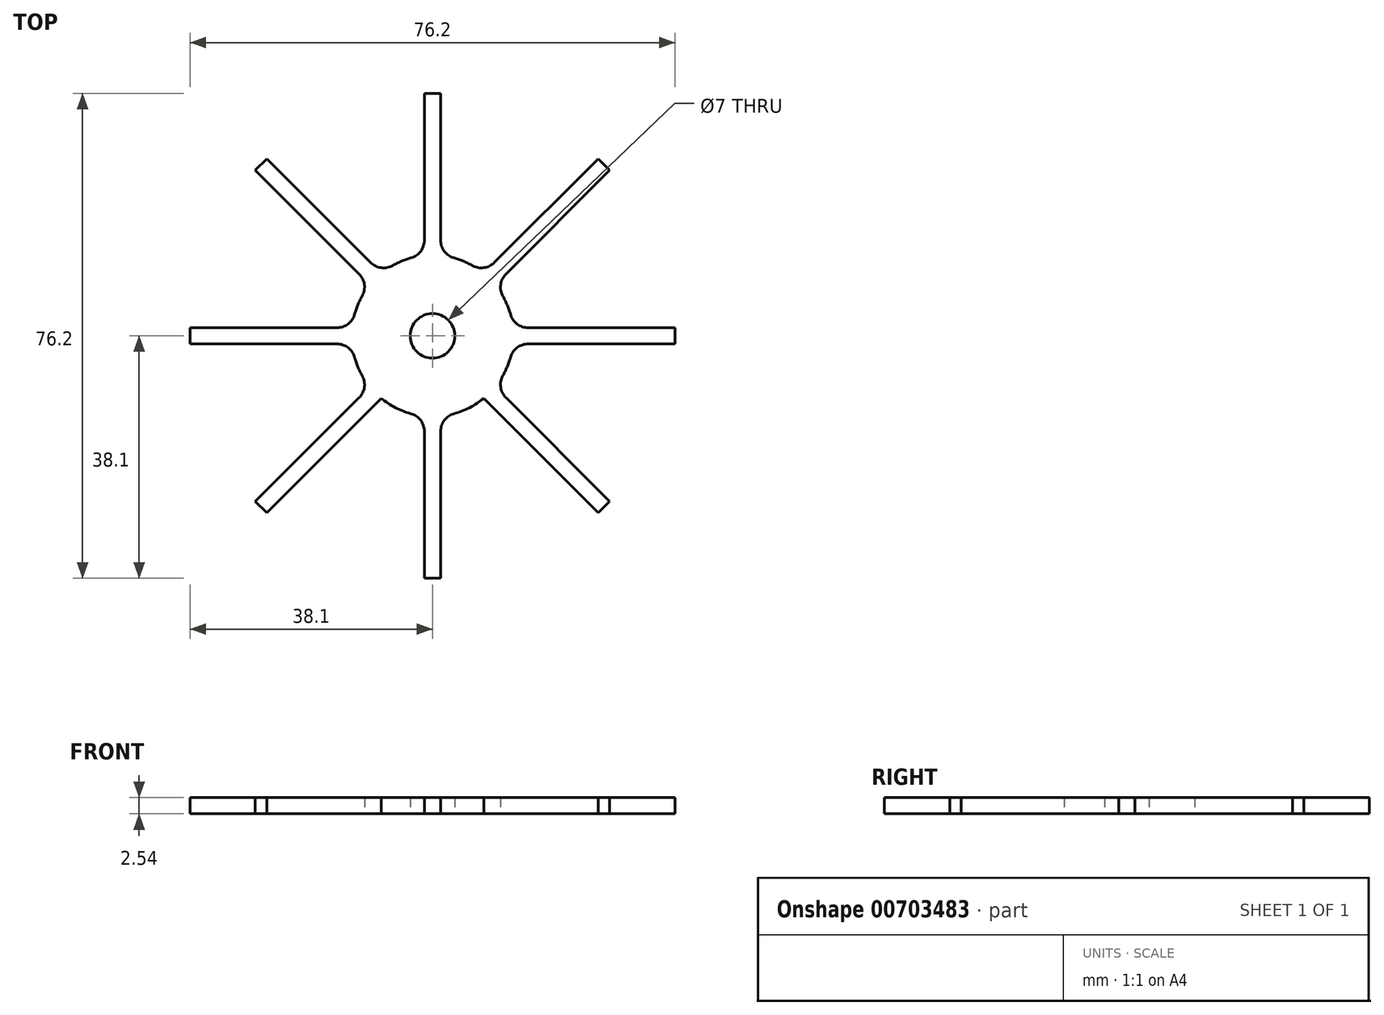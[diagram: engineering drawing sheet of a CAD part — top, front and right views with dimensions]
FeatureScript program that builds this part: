
annotation { "Feature Type Name" : "Feature", "Feature Type Description" : "" }
export const myFeature = defineFeature(function(context is Context, id is Id, definition is map)
    precondition{}
    {
        {
            var Q0;
            Q0=qCreatedBy(makeId("Top.planeOp"),FACE);
            var sketch = newSketch(context, id + "F0", { "sketchPlane" : qUnion([Q0])});
            skCircle(sketch, "E0", {"center": v(0, 0) * mm, "radius": 12.7 * mm});
            skSolve(sketch);
        }
        {
            var Q0;
            Q0=makeQuery(id+"F0.imprint","IMPRINT",FACE,{"disambiguationData":[TD([[makeQuery(id+"F0.imprint","IMPRINT",EDGE,{"derivedFrom":sQuery(id+"F0.wireOp",EDGE,"E0")}),1.0]])]});
            extrude(context, id + "F1", {"entities" : qUnion([Q0]), "depth" : 2.54 * mm, "offsetDistance" : 25.4 * mm});
        }
        {
            var Q0;
            Q0=qCreatedBy(makeId("Top.planeOp"),FACE);
            var sketch = newSketch(context, id + "F2", { "sketchPlane" : qUnion([Q0])});
            skLineSegment(sketch, "E1.bottom", {"start": v(-1.27, -38.1) * mm, "end": v(1.27, -38.1) * mm});
            skLineSegment(sketch, "E1.top", {"start": v(-1.27, 38.1) * mm, "end": v(1.27, 38.1) * mm});
            skLineSegment(sketch, "E1.left", {"start": v(-1.27, -38.1) * mm, "end": v(-1.27, 38.1) * mm});
            skLineSegment(sketch, "E1.right", {"start": v(1.27, -38.1) * mm, "end": v(1.27, 38.1) * mm});
            skPoint(sketch, "E1.middle", {"position": v(0, 0) * mm});
            skSolve(sketch);
        }
        {
            var Q0;
            Q0=makeQuery(id+"F2.imprint","IMPRINT",FACE,{"disambiguationData":[TD([[makeQuery(id+"F2.imprint","IMPRINT",EDGE,{"derivedFrom":sQuery(id+"F2.wireOp",EDGE,"E1.bottom")}),1.0]])]});
            extrude(context, id + "F3", {"entities" : qUnion([Q0]), "operationType" : NewBodyOperationType.ADD, "depth" : 2.54 * mm, "offsetDistance" : 25.4 * mm});
        }
        {
            var Q0;
            Q0=qCreatedBy(makeId("Top.planeOp"),FACE);
            var sketch = newSketch(context, id + "F4", { "sketchPlane" : qUnion([Q0])});
            skLineSegment(sketch, "E2.bottom", {"start": v(-38.1, -1.27) * mm, "end": v(38.1, -1.27) * mm});
            skLineSegment(sketch, "E2.top", {"start": v(-38.1, 1.27) * mm, "end": v(38.1, 1.27) * mm});
            skLineSegment(sketch, "E2.left", {"start": v(-38.1, -1.27) * mm, "end": v(-38.1, 1.27) * mm});
            skLineSegment(sketch, "E2.right", {"start": v(38.1, -1.27) * mm, "end": v(38.1, 1.27) * mm});
            skPoint(sketch, "E2.middle", {"position": v(0, 0) * mm});
            skSolve(sketch);
        }
        {
            var Q0;
            Q0 = qSketchRegion(id + "F4", true);
            extrude(context, id + "F5", {"entities" : qUnion([Q0]), "operationType" : NewBodyOperationType.ADD, "depth" : 2.54 * mm, "offsetDistance" : 25.4 * mm});
        }
        {
            var Q0;
            Q0=qCreatedBy(makeId("Top.planeOp"),FACE);
            var sketch = newSketch(context, id + "F6", { "sketchPlane" : qUnion([Q0])});
            skLineSegment(sketch, "E3", {"start": v(0, 0) * mm, "end": v(-0.9, 0.9) * mm});
            skLineSegment(sketch, "E4", {"start": v(-0.9, 0.9) * mm, "end": v(0.9, -0.9) * mm});
            skLineSegment(sketch, "E5", {"start": v(26.04, 27.84) * mm, "end": v(-0.9, 0.9) * mm});
            skLineSegment(sketch, "E6", {"start": v(27.84, 26.04) * mm, "end": v(0.9, -0.9) * mm});
            skLineSegment(sketch, "E7", {"start": v(26.04, 27.84) * mm, "end": v(27.84, 26.04) * mm});
            skSolve(sketch);
        }
        {
            var Q0;
            {var subQ0=sQuery(id+"F6.wireOp",EDGE,"E5");Q0=makeQuery(id+"F6.imprint","IMPRINT",FACE,{"disambiguationData":[TD([[makeQuery(id+"F6.imprint","IMPRINT",EDGE,{"derivedFrom":subQ0}),1.0]])]});}
            extrude(context, id + "F7", {"entities" : qUnion([Q0]), "operationType" : NewBodyOperationType.ADD, "depth" : 2.54 * mm, "offsetDistance" : 25.4 * mm});
        }
        {
            var Q0;
            Q0=makeQuery(id+"F1.opExtrude","SWEPT_BODY",BODY,{"disambiguationData":[OSD([sQuery(id+"F0.wireOp",EDGE,"E0")])]});
            var Q1;
            Q1=qCreatedBy(makeId("Front.planeOp"),FACE);
            mirror(context, id + "F8", {"operationType" : NewBodyOperationType.ADD, "entities" : qUnion([Q0]), "mirrorPlane" : qUnion([Q1])});
        }
        {
            var Q0;
            Q0=makeQuery(id+"F1.opExtrude","SWEPT_BODY",BODY,{"disambiguationData":[OSD([sQuery(id+"F0.wireOp",EDGE,"E0")])]});
            var Q1;
            Q1=qCreatedBy(makeId("Right.planeOp"),FACE);
            mirror(context, id + "F9", {"operationType" : NewBodyOperationType.ADD, "entities" : qUnion([Q0]), "mirrorPlane" : qUnion([Q1])});
        }
        {
            var Q0;
            Q0=qCreatedBy(makeId("Top.planeOp"),FACE);
            var sketch = newSketch(context, id + "F10", { "sketchPlane" : qUnion([Q0])});
            skCircle(sketch, "E8", {"center": v(0, 0) * mm, "radius": 3.5 * mm});
            skSolve(sketch);
        }
        {
            var Q0;
            Q0=makeQuery(id+"F10.imprint","IMPRINT",FACE,{"disambiguationData":[TD([[makeQuery(id+"F10.imprint","IMPRINT",EDGE,{"derivedFrom":sQuery(id+"F10.wireOp",EDGE,"E8")}),1.0]])]});
            extrude(context, id + "F11", {"entities" : qUnion([Q0]), "operationType" : NewBodyOperationType.REMOVE, "depth" : 14.73 * mm, "offsetDistance" : 25.4 * mm});
        }
        {
            var Q0;
            {var subQ0=sQuery(id+"F2.wireOp",EDGE,"E1.right");var subQ4=sQuery(id+"F0.wireOp",EDGE,"E0");Q0=makeQuery(id+"F5.boolean.opBoolean","INTERSECT",EDGE,{"derivedFrom":[makeQuery(id+"F3.boolean.opBoolean","SPLIT",FACE,{"disambiguationData":[TD([makeQuery(id+"F3.opExtrude","SWEPT_FACE",FACE,{"disambiguationData":[OSD([subQ0])]})])],"derivedFrom":makeQuery(id+"F1.opExtrude","SWEPT_FACE",FACE,{"disambiguationData":[OSD([subQ4])]})}),makeQuery(id+"F5.opExtrude","SWEPT_FACE",FACE,{"disambiguationData":[OSD([sQuery(id+"F4.wireOp",EDGE,"E2.top")])]})]});}
            var Q1;
            {var subQ0=sQuery(id+"F2.wireOp",EDGE,"E1.right");var subQ6=sQuery(id+"F0.wireOp",EDGE,"E0");var subQ9=makeQuery(id+"F3.opExtrude","SWEPT_FACE",FACE,{"disambiguationData":[OSD([subQ0])]});var subQ12=sQuery(id+"F4.wireOp",EDGE,"E2.top");Q1=makeQuery(id+"F7.boolean.opBoolean","INTERSECT",EDGE,{"derivedFrom":[makeQuery(id+"F5.boolean.opBoolean","SPLIT",FACE,{"disambiguationData":[TD([makeQuery(id+"F5.opExtrude","SWEPT_FACE",FACE,{"disambiguationData":[OSD([subQ12])]})])],"derivedFrom":makeQuery(id+"F3.boolean.opBoolean","SPLIT",FACE,{"disambiguationData":[TD([subQ9])],"derivedFrom":makeQuery(id+"F1.opExtrude","SWEPT_FACE",FACE,{"disambiguationData":[OSD([subQ6])]})})}),makeQuery(id+"F7.opExtrude","SWEPT_FACE",FACE,{"disambiguationData":[OSD([sQuery(id+"F6.wireOp",EDGE,"E6")])]})]});}
            var Q2;
            Q2=makeQuery(id+"F3.boolean.opBoolean","INTERSECT",EDGE,{"disambiguationData":[OD(1.0)],"derivedFrom":[makeQuery(id+"F1.opExtrude","SWEPT_FACE",FACE,{"disambiguationData":[OSD([sQuery(id+"F0.wireOp",EDGE,"E0")])]}),makeQuery(id+"F3.opExtrude","SWEPT_FACE",FACE,{"disambiguationData":[OSD([sQuery(id+"F2.wireOp",EDGE,"E1.right")])]})]});
            var Q3;
            {var subQ0=sQuery(id+"F2.wireOp",EDGE,"E1.right");var subQ6=sQuery(id+"F0.wireOp",EDGE,"E0");var subQ9=makeQuery(id+"F3.opExtrude","SWEPT_FACE",FACE,{"disambiguationData":[OSD([subQ0])]});var subQ12=sQuery(id+"F4.wireOp",EDGE,"E2.top");Q3=makeQuery(id+"F7.boolean.opBoolean","INTERSECT",EDGE,{"derivedFrom":[makeQuery(id+"F5.boolean.opBoolean","SPLIT",FACE,{"disambiguationData":[TD([makeQuery(id+"F5.opExtrude","SWEPT_FACE",FACE,{"disambiguationData":[OSD([subQ12])]})])],"derivedFrom":makeQuery(id+"F3.boolean.opBoolean","SPLIT",FACE,{"disambiguationData":[TD([subQ9])],"derivedFrom":makeQuery(id+"F1.opExtrude","SWEPT_FACE",FACE,{"disambiguationData":[OSD([subQ6])]})})}),makeQuery(id+"F7.opExtrude","SWEPT_FACE",FACE,{"disambiguationData":[OSD([sQuery(id+"F6.wireOp",EDGE,"E5")])]})]});}
            var Q4;
            {var subQ0=sQuery(id+"F2.wireOp",EDGE,"E1.right");var subQ4=sQuery(id+"F0.wireOp",EDGE,"E0");Q4=makeQuery(id+"F5.boolean.opBoolean","INTERSECT",EDGE,{"derivedFrom":[makeQuery(id+"F3.boolean.opBoolean","SPLIT",FACE,{"disambiguationData":[TD([makeQuery(id+"F3.opExtrude","SWEPT_FACE",FACE,{"disambiguationData":[OSD([subQ0])]})])],"derivedFrom":makeQuery(id+"F1.opExtrude","SWEPT_FACE",FACE,{"disambiguationData":[OSD([subQ4])]})}),makeQuery(id+"F5.opExtrude","SWEPT_FACE",FACE,{"disambiguationData":[OSD([sQuery(id+"F4.wireOp",EDGE,"E2.bottom")])]})]});}
            var Q5;
            {var subQ0=sQuery(id+"F2.wireOp",EDGE,"E1.right");var subQ6=sQuery(id+"F0.wireOp",EDGE,"E0");var subQ9=makeQuery(id+"F3.opExtrude","SWEPT_FACE",FACE,{"disambiguationData":[OSD([subQ0])]});var subQ12=sQuery(id+"F4.wireOp",EDGE,"E2.top");Q5=makeQuery(id+"F8.opPattern","COPY",EDGE,{"derivedFrom":makeQuery(id+"F7.boolean.opBoolean","INTERSECT",EDGE,{"derivedFrom":[makeQuery(id+"F5.boolean.opBoolean","SPLIT",FACE,{"disambiguationData":[TD([makeQuery(id+"F5.opExtrude","SWEPT_FACE",FACE,{"disambiguationData":[OSD([subQ12])]})])],"derivedFrom":makeQuery(id+"F3.boolean.opBoolean","SPLIT",FACE,{"disambiguationData":[TD([subQ9])],"derivedFrom":makeQuery(id+"F1.opExtrude","SWEPT_FACE",FACE,{"disambiguationData":[OSD([subQ6])]})})}),makeQuery(id+"F7.opExtrude","SWEPT_FACE",FACE,{"disambiguationData":[OSD([sQuery(id+"F6.wireOp",EDGE,"E6")])]})]}),"instanceName":"1"});}
            fillet(context, id + "F12", {"entities" : qUnion([Q0, Q1, Q2, Q3, Q4, Q5]), "radius" : 2.92 * mm, "tangentPropagation" : true, "allowEdgeOverflow" : false});
        }
        {
            var Q0;
            Q0=makeQuery(id+"F3.boolean.opBoolean","INTERSECT",EDGE,{"disambiguationData":[OD(0.0)],"derivedFrom":[makeQuery(id+"F1.opExtrude","SWEPT_FACE",FACE,{"disambiguationData":[OSD([sQuery(id+"F0.wireOp",EDGE,"E0")])]}),makeQuery(id+"F3.opExtrude","SWEPT_FACE",FACE,{"disambiguationData":[OSD([sQuery(id+"F2.wireOp",EDGE,"E1.right")])]})]});
            var Q1;
            {var subQ0=sQuery(id+"F2.wireOp",EDGE,"E1.right");var subQ6=sQuery(id+"F0.wireOp",EDGE,"E0");var subQ9=makeQuery(id+"F3.opExtrude","SWEPT_FACE",FACE,{"disambiguationData":[OSD([subQ0])]});var subQ12=sQuery(id+"F4.wireOp",EDGE,"E2.top");Q1=makeQuery(id+"F8.opPattern","COPY",EDGE,{"derivedFrom":makeQuery(id+"F7.boolean.opBoolean","INTERSECT",EDGE,{"derivedFrom":[makeQuery(id+"F5.boolean.opBoolean","SPLIT",FACE,{"disambiguationData":[TD([makeQuery(id+"F5.opExtrude","SWEPT_FACE",FACE,{"disambiguationData":[OSD([subQ12])]})])],"derivedFrom":makeQuery(id+"F3.boolean.opBoolean","SPLIT",FACE,{"disambiguationData":[TD([subQ9])],"derivedFrom":makeQuery(id+"F1.opExtrude","SWEPT_FACE",FACE,{"disambiguationData":[OSD([subQ6])]})})}),makeQuery(id+"F7.opExtrude","SWEPT_FACE",FACE,{"disambiguationData":[OSD([sQuery(id+"F6.wireOp",EDGE,"E5")])]})]}),"instanceName":"1"});}
            fillet(context, id + "F13", {"entities" : qUnion([Q0, Q1]), "radius" : 2.91 * mm, "tangentPropagation" : true, "allowEdgeOverflow" : false});
        }
        {
            var Q0;
            Q0=makeQuery(id+"F1.opExtrude","SWEPT_BODY",BODY,{"disambiguationData":[OSD([sQuery(id+"F0.wireOp",EDGE,"E0")])]});
            var Q1;
            Q1=qCreatedBy(makeId("Right.planeOp"),FACE);
            mirror(context, id + "F14", {"operationType" : NewBodyOperationType.ADD, "entities" : qUnion([Q0]), "mirrorPlane" : qUnion([Q1])});
        }
    });
